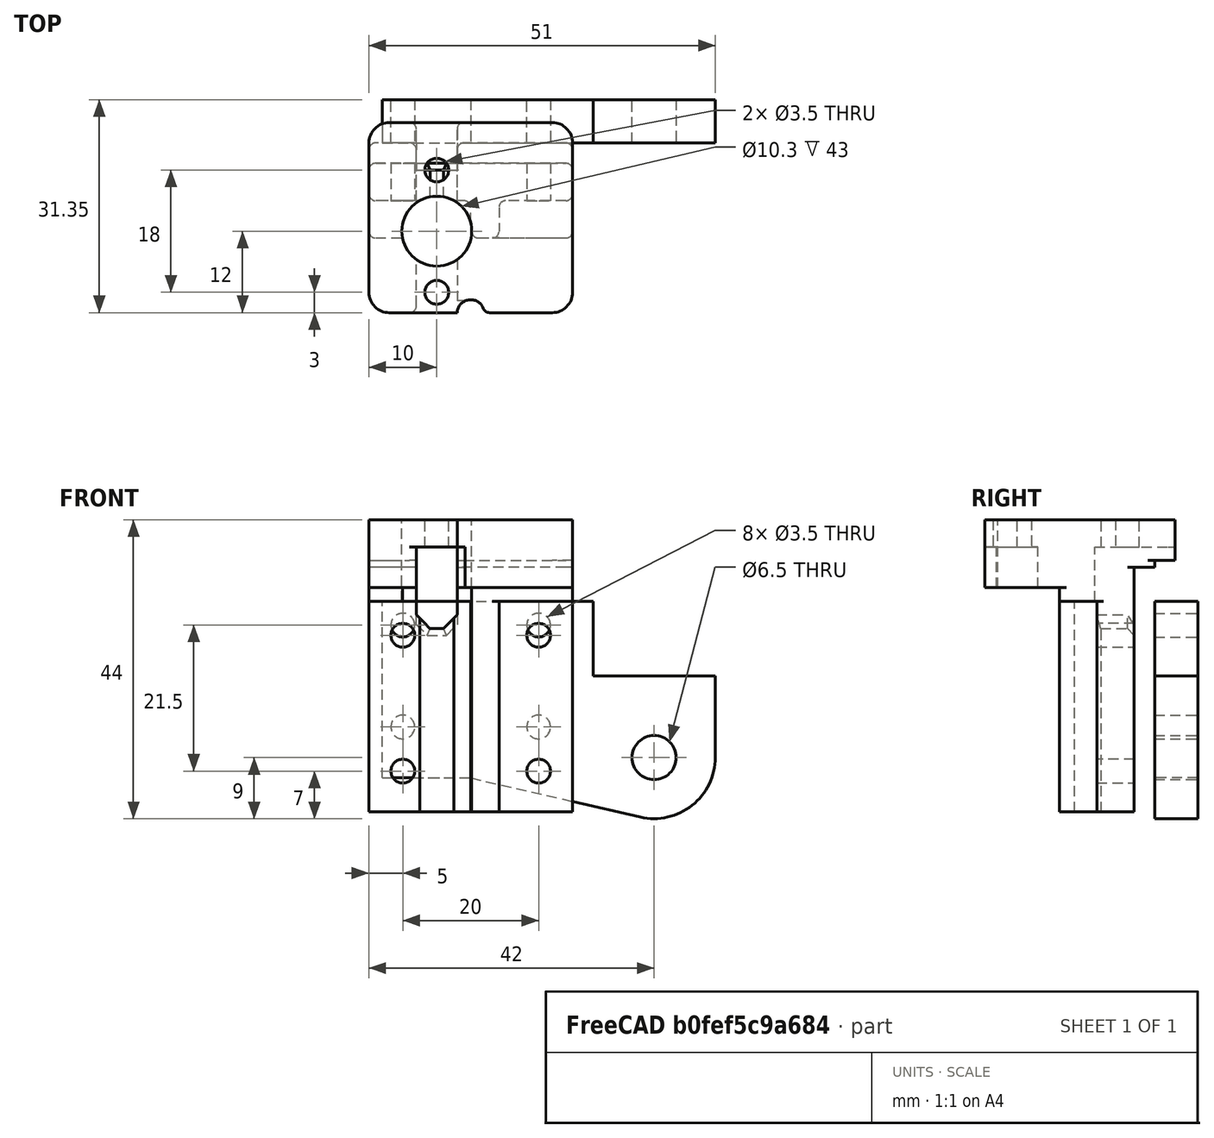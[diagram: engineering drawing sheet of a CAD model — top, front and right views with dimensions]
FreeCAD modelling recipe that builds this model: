
FCSTD DOCUMENT  (FreeCAD 0.19R)
Label: ZnutHolder_H3
License: All rights reserved
LicenseURL: http://en.wikipedia.org/wiki/All_rights_reserved
objects: PartDesign::Fillet×14, Sketcher::SketchObject×11, PartDesign::Pocket×8, PartDesign::Chamfer×3, PartDesign::Pad×2, PartDesign::Body×2, Mesh::Feature×1
note: 67 computed .brp shape members not serialized (recipe doc carries the construction recipe); baked Part::Feature solids carry a one-line shape summary decoded from their .brp

FEATURE [Sketcher::SketchObject] Sketch
  FullyConstrained = false
  MapMode = 5
  Placement = pos=(0,0,0) rot=(1,0,0;1.5708rad)
  Support = -> [XZ_Plane]
  sketch-geometry (14):
    g0: Circle CenterX=-10 CenterY=7.5 CenterZ=0 NormalX=0 NormalY=0 NormalZ=1 AngleXU=0 Radius=1.75
    g1: Circle CenterX=10 CenterY=7.5 CenterZ=0 NormalX=0 NormalY=0 NormalZ=1 AngleXU=0 Radius=1.75
    g2: Circle CenterX=-10 CenterY=-7.5 CenterZ=0 NormalX=0 NormalY=0 NormalZ=1 AngleXU=0 Radius=1.75
    g3: Circle CenterX=10 CenterY=-7.5 CenterZ=0 NormalX=0 NormalY=0 NormalZ=1 AngleXU=0 Radius=1.75
    g4: LineSegment StartX=-13 StartY=11 StartZ=0 EndX=18 EndY=11 EndZ=0
    g5: LineSegment StartX=18 StartY=11 StartZ=0 EndX=18 EndY=0 EndZ=0
    g6: LineSegment StartX=18 StartY=0 StartZ=0 EndX=36 EndY=0 EndZ=0
    g7: LineSegment StartX=36 StartY=0 StartZ=0 EndX=36 EndY=-12 EndZ=0
    g8: LineSegment StartX=-13 StartY=-15 StartZ=0 EndX=-13 EndY=11 EndZ=0
    g9: LineSegment StartX=-13 StartY=-15 StartZ=0 EndX=0 EndY=-15 EndZ=0
    g10: LineSegment StartX=0 StartY=-15 StartZ=0 EndX=24.9743 EndY=-20.7691 EndZ=0
    g11: ArcOfCircle CenterX=27 CenterY=-12 CenterZ=0 NormalX=0 NormalY=0 NormalZ=1 AngleXU=0 Radius=9 StartAngle=4.48537 EndAngle=6.28319
    g12: Circle CenterX=27 CenterY=-12 CenterZ=0 NormalX=0 NormalY=0 NormalZ=1 AngleXU=0 Radius=3.25
    g13: LineSegment StartX=19 StartY=18.0628 StartZ=0 EndX=19 EndY=-24.6673 EndZ=0
  constraints (37):
    c: Symmetric(g0,g1,g-2)
    c: Symmetric(g3,g2,g-2)
    c: Symmetric(g3,g1,g-1)
    c: Diameter(g0) = 3.5
    c: Equal(g0,g1)
    c: Equal(g0,g2)
    c: Equal(g0,g3)
    c: Distance(g1,g0) = 20
    c: Distance(g3,g1) = 15
    c: Horizontal(g4)
    c: Coincident(g4,g5)
    c: Vertical(g5)
    c: Coincident(g5,g6)
    c: Horizontal(g6)
    c: Coincident(g6,g7)
    c: Vertical(g7)
    c: Vertical(g8)
    c: DistanceX(g4) = 18
    c: DistanceX(g4) = -13
    c: Coincident(g8,g9)
    c: PointOnObject(g9,g-2)
    c: Horizontal(g9)
    c: Coincident(g9,g10)
    c: Tangent(g7,g11) = 1.5708
    c: Coincident(g11,g7)
    c: Tangent(g11,g10) = -1.5708
    c: Coincident(g12,g11)
    c: Diameter(g12) = 6.5
    c: Diameter(g11) = 18
    c: Vertical(g13)
    c: DistanceX(g13) = 19
    c: Distance(g11,g13) = 8
    c: Distance(g11,g6) = 12
    c: PointOnObject(g5,g-1)
    c: Coincident(g8,g4)
    c: DistanceY(g4) = 11
    c: DistanceY(g8) = -15
FEATURE [PartDesign::Pad] Pad
  Direction = (1,1,1)
  Length = 6.35
  Length2 = 100
  Placement = pos=(0,0,0) rot=(1,0,0;1.5708rad)
  Profile = -> Sketch
  Type = 0
FEATURE [PartDesign::Body] Body  label="Tab"
  Group = -> [Sketch,Pad]
  Origin = -> Origin
  Placement = pos=(0,6.35,0) rot=(0,0,1;0rad)
  Tip = -> Pad
FEATURE [Sketcher::SketchObject] Sketch005  label="body"
  FullyConstrained = true
  MapMode = 5
  Placement = pos=(0,0,0) rot=(0.57735,0.57735,0.57735;2.0944rad)
  Support = -> [YZ_Plane001]
  sketch-geometry (8):
    g0: LineSegment StartX=0 StartY=-20 StartZ=0 EndX=0 EndY=17 EndZ=0
    g1: LineSegment StartX=0 StartY=17 StartZ=0 EndX=3 EndY=17 EndZ=0
    g2: LineSegment StartX=3 StartY=17 StartZ=0 EndX=3 EndY=23 EndZ=0
    g3: LineSegment StartX=3 StartY=23 StartZ=0 EndX=-25 EndY=23 EndZ=0
    g4: LineSegment StartX=-25 StartY=23 StartZ=0 EndX=-25 EndY=13 EndZ=0
    g5: LineSegment StartX=-25 StartY=13 StartZ=0 EndX=-14 EndY=13 EndZ=0
    g6: LineSegment StartX=-14 StartY=13 StartZ=0 EndX=-14 EndY=-20 EndZ=0
    g7: LineSegment StartX=-14 StartY=-20 StartZ=0 EndX=0 EndY=-20 EndZ=0
  constraints (24):
    c: PointOnObject(g0,g-2)
    c: PointOnObject(g0,g-2)
    c: Coincident(g0,g1)
    c: Coincident(g1,g2)
    c: Vertical(g2)
    c: Coincident(g2,g3)
    c: Horizontal(g3)
    c: Coincident(g3,g4)
    c: Vertical(g4)
    c: Coincident(g4,g5)
    c: Horizontal(g5)
    c: Coincident(g5,g6)
    c: Vertical(g6)
    c: Coincident(g6,g7)
    c: Coincident(g7,g0)
    c: Horizontal(g7)
    c: Distance(g4) = 10
    c: DistanceY(g2) = 23
    c: DistanceX(g4) = -25
    c: Distance(g7) = 14
    c: DistanceY(g0) = -20
    c: DistanceX(g2) = 3
    c: Horizontal(g1)
    c: Distance(g2) = 6
FEATURE [PartDesign::Pad] Pad001
  Direction = (1,1,1)
  Length = 15
  Length2 = 15
  Placement = pos=(0,0,0) rot=(0.57735,0.57735,0.57735;2.0944rad)
  Profile = -> Sketch005
  Type = 4
FEATURE [Sketcher::SketchObject] Sketch007  label="ScrewHoles_rail"
  FullyConstrained = true
  MapMode = 5
  Placement = pos=(-6.2e-15,-14,2.33e-14) rot=(0.57735,0.57735,-0.57735;2.0944rad)
  sketch-geometry (8):
    g0: Circle CenterX=-6 CenterY=10 CenterZ=0 NormalX=0 NormalY=0 NormalZ=1 AngleXU=0 Radius=1.75
    g1: Circle CenterX=14 CenterY=10 CenterZ=0 NormalX=0 NormalY=0 NormalZ=1 AngleXU=0 Radius=1.75
    g2: Circle CenterX=-6 CenterY=-10 CenterZ=0 NormalX=0 NormalY=0 NormalZ=1 AngleXU=0 Radius=1.75
    g3: Circle CenterX=14 CenterY=-10 CenterZ=0 NormalX=0 NormalY=0 NormalZ=1 AngleXU=0 Radius=1.75
    g4: LineSegment StartX=-6 StartY=10 StartZ=0 EndX=-6 EndY=-10 EndZ=0
    g5: LineSegment StartX=-6 StartY=-10 StartZ=0 EndX=14 EndY=-10 EndZ=0
    g6: LineSegment StartX=14 StartY=-10 StartZ=0 EndX=14 EndY=10 EndZ=0
    g7: LineSegment StartX=14 StartY=10 StartZ=0 EndX=-6 EndY=10 EndZ=0
  constraints (19):
    c: Diameter(g0) = 3.5
    c: Equal(g0,g1)
    c: Equal(g0,g2)
    c: Equal(g0,g3)
    c: Coincident(g4,g0)
    c: Coincident(g4,g2)
    c: Coincident(g4,g5)
    c: Coincident(g5,g3)
    c: Coincident(g5,g6)
    c: Coincident(g6,g1)
    c: Coincident(g6,g7)
    c: Coincident(g7,g4)
    c: Equal(g4,g6)
    c: Equal(g7,g5)
    c: Distance(g7) = 20
    c: Distance(g6) = 20
    c: Perpendicular(g6,g5)
    c: Symmetric(g1,g3,g-1)
    c: DistanceX(g0) = -6
FEATURE [Sketcher::SketchObject] Sketch008  label="ScrewRelief"
  FullyConstrained = false
  MapMode = 5
  Placement = pos=(2.11e-14,-1.55e-14,-20) rot=(0.707107,0.707107,0;3.14159rad)
  sketch-geometry (8):
    g0: LineSegment StartX=-14.9077 StartY=0 StartZ=0 EndX=-8.5 EndY=0 EndZ=0
    g1: LineSegment StartX=-8.5 StartY=0 StartZ=0 EndX=-8.5 EndY=-16 EndZ=0
    g2: LineSegment StartX=-8.5 StartY=-16 StartZ=0 EndX=-14.9077 EndY=-16 EndZ=0
    g3: LineSegment StartX=-14.9077 StartY=-16 StartZ=0 EndX=-14.9077 EndY=0 EndZ=0
    g4: LineSegment StartX=-15.43 StartY=17.5817 StartZ=0 EndX=-8.5 EndY=17.5817 EndZ=0
    g5: LineSegment StartX=-8.5 StartY=17.5817 StartZ=0 EndX=-8.5 EndY=4.16376 EndZ=0
    g6: LineSegment StartX=-8.5 StartY=4.16376 StartZ=0 EndX=-15.43 EndY=4.16376 EndZ=0
    g7: LineSegment StartX=-15.43 StartY=4.16376 StartZ=0 EndX=-15.43 EndY=17.5817 EndZ=0
  constraints (20):
    c: Coincident(g0,g1)
    c: Coincident(g1,g2)
    c: Coincident(g2,g3)
    c: Coincident(g3,g0)
    c: Horizontal(g0)
    c: Horizontal(g2)
    c: Vertical(g1)
    c: Vertical(g3)
    c: Distance(g1) = 16
    c: DistanceY(g0) = 0
    c: DistanceX(g1) = -8.5
    c: Coincident(g4,g5)
    c: Coincident(g5,g6)
    c: Coincident(g6,g7)
    c: Coincident(g7,g4)
    c: Horizontal(g4)
    c: Horizontal(g6)
    c: Vertical(g5)
    c: Vertical(g7)
    c: DistanceX(g4) = -8.5
FEATURE [Sketcher::SketchObject] Sketch011  label="Carriage"
  FullyConstrained = false
  MapMode = 5
  Placement = pos=(0,0,0) rot=(1,0,0;1.5708rad)
  Support = -> [XZ_Plane001]
  sketch-geometry (8):
    g0: LineSegment StartX=-19.4447 StartY=17.5 StartZ=0 EndX=25.2288 EndY=17.5 EndZ=0
    g1: LineSegment StartX=25.2288 StartY=17.5 StartZ=0 EndX=25.2288 EndY=-17.5 EndZ=0
    g2: LineSegment StartX=25.2288 StartY=-17.5 StartZ=0 EndX=-19.4447 EndY=-17.5 EndZ=0
    g3: LineSegment StartX=-19.4447 StartY=-17.5 StartZ=0 EndX=-19.4447 EndY=17.5 EndZ=0
    g4: LineSegment StartX=-16.964 StartY=15 StartZ=0 EndX=21.1039 EndY=15 EndZ=0
    g5: LineSegment StartX=21.1039 StartY=15 StartZ=0 EndX=21.1039 EndY=-15 EndZ=0
    g6: LineSegment StartX=21.1039 StartY=-15 StartZ=0 EndX=-16.964 EndY=-15 EndZ=0
    g7: LineSegment StartX=-16.964 StartY=-15 StartZ=0 EndX=-16.964 EndY=15 EndZ=0
  constraints (19):
    c: Coincident(g0,g1)
    c: Coincident(g1,g2)
    c: Coincident(g2,g3)
    c: Coincident(g3,g0)
    c: Horizontal(g0)
    c: Horizontal(g2)
    c: Vertical(g1)
    c: Vertical(g3)
    c: DistanceY(g0) = 17.5
    c: Distance(g1) = 35
    c: Coincident(g4,g5)
    c: Coincident(g5,g6)
    c: Coincident(g6,g7)
    c: Coincident(g7,g4)
    c: Horizontal(g4)
    c: Horizontal(g6)
    c: Vertical(g7)
    c: Distance(g5) = 30
    c: Symmetric(g4,g5,g-1)
FEATURE [Sketcher::SketchObject] Sketch012  label="NutHole"
  FullyConstrained = true
  MapMode = 5
  Placement = pos=(-8.9e-15,1.28e-14,23) rot=(0,0,-1;1.5708rad)
  Support = -> [Pad001]
  sketch-geometry (1):
    g0: Circle CenterX=13 CenterY=-5 CenterZ=0 NormalX=0 NormalY=0 NormalZ=1 AngleXU=0 Radius=5.15
  constraints (3):
    c: Diameter(g0) = 10.3
    c: DistanceY(g0) = -5
    c: DistanceX(g0) = 13
FEATURE [Sketcher::SketchObject] Sketch013  label="Nutscrews"
  FullyConstrained = true
  MapMode = 5
  Placement = pos=(-7.2e-14,3.9e-14,35) rot=(0,0,-1;1.5708rad)
  sketch-geometry (2):
    g0: Circle CenterX=4 CenterY=-5 CenterZ=0 NormalX=0 NormalY=0 NormalZ=1 AngleXU=0 Radius=1.75
    g1: Circle CenterX=22 CenterY=-5 CenterZ=0 NormalX=0 NormalY=0 NormalZ=1 AngleXU=0 Radius=1.75
  constraints (6):
    c: DistanceY(g1) = -5
    c: DistanceY(g0) = -5
    c: DistanceX(g1) = 22
    c: DistanceX(g0) = 4
    c: Diameter(g1) = 3.5
    c: Equal(g1,g0)
FEATURE [Sketcher::SketchObject] Sketch014  label="tunnel"
  ExternalGeometry = -> [Pad001]
  FullyConstrained = true
  MapMode = 5
  Placement = pos=(-1.11e-14,-25,8.3e-15) rot=(-0.57735,-0.57735,0.57735;4.18879rad)
  Support = -> [Pad001]
  sketch-geometry (4):
    g0: LineSegment StartX=-19 StartY=-2 StartZ=0 EndX=-7 EndY=-2 EndZ=0
    g1: LineSegment StartX=-7 StartY=-2 StartZ=0 EndX=-7 EndY=-8 EndZ=0
    g2: LineSegment StartX=-7 StartY=-8 StartZ=0 EndX=-19 EndY=-8 EndZ=0
    g3: LineSegment StartX=-19 StartY=-8 StartZ=0 EndX=-19 EndY=-2 EndZ=0
  constraints (12):
    c: Coincident(g0,g1)
    c: Coincident(g1,g2)
    c: Coincident(g2,g3)
    c: Coincident(g3,g0)
    c: Horizontal(g0)
    c: Horizontal(g2)
    c: Vertical(g1)
    c: Vertical(g3)
    c: Distance(g1) = 6
    c: DistanceY(g0) = -2
    c: Distance(g0) = 12
    c: Distance(g0,g-3) = 4
FEATURE [PartDesign::Pocket] Pocket
  BaseFeature = -> Pad001
  Length = 5
  Length2 = 100
  Placement = pos=(0,0,0) rot=(0.57735,0.57735,0.57735;2.0944rad)
  Profile = -> Sketch014
  Type = 1
FEATURE [Sketcher::SketchObject] Sketch015  label="backpocket"
  FullyConstrained = true
  MapMode = 5
  Placement = pos=(0,-8e-15,0) rot=(0.57735,0.57735,0.57735;4.18879rad)
  sketch-geometry (4):
    g0: LineSegment StartX=-34.47 StartY=20 StartZ=0 EndX=16 EndY=20 EndZ=0
    g1: LineSegment StartX=16 StartY=20 StartZ=0 EndX=16 EndY=-20 EndZ=0
    g2: LineSegment StartX=16 StartY=-20 StartZ=0 EndX=-34.47 EndY=-20 EndZ=0
    g3: LineSegment StartX=-34.47 StartY=-20 StartZ=0 EndX=-34.47 EndY=20 EndZ=0
  constraints (11):
    c: Coincident(g0,g1)
    c: Coincident(g1,g2)
    c: Coincident(g2,g3)
    c: Coincident(g3,g0)
    c: Horizontal(g0)
    c: Horizontal(g2)
    c: Vertical(g1)
    c: Distance(g3) = 40
    c: Symmetric(g2,g0,g-1)
    c: Distance(g0) = 50.47
    c: DistanceX(g0) = 16
FEATURE [Sketcher::SketchObject] Sketch018  label="Seamnotch"
  FullyConstrained = false
  MapMode = 5
  Placement = pos=(-9.8e-15,3.48e-14,35) rot=(0,0,-1;1.5708rad)
  sketch-geometry (1):
    g0: Circle CenterX=25.0896 CenterY=0 CenterZ=0 NormalX=0 NormalY=0 NormalZ=1 AngleXU=0 Radius=2
  constraints (2):
    c: PointOnObject(g0,g-1)
    c: Diameter(g0) = 4
FEATURE [PartDesign::Pocket] Pocket001
  BaseFeature = -> Pocket
  Length = 21
  Length2 = 100
  Placement = pos=(0,0,0) rot=(0.57735,0.57735,0.57735;2.0944rad)
  Profile = -> Sketch013
  Type = 0
FEATURE [PartDesign::Pocket] Pocket002
  BaseFeature = -> Pocket001
  Length = 15
  Length2 = 100
  Placement = pos=(0,0,0) rot=(0.57735,0.57735,0.57735;2.0944rad)
  Profile = -> Sketch012
  Type = 1
FEATURE [PartDesign::Pocket] Pocket003
  BaseFeature = -> Pocket002
  Length = 5
  Length2 = 100
  Placement = pos=(0,0,0) rot=(0.57735,0.57735,0.57735;2.0944rad)
  Profile = -> Sketch007
  Type = 1
FEATURE [PartDesign::Pocket] Pocket004
  BaseFeature = -> Pocket003
  Length = 31
  Length2 = 100
  Placement = pos=(0,0,0) rot=(0.57735,0.57735,0.57735;2.0944rad)
  Profile = -> Sketch008
  Type = 0
FEATURE [PartDesign::Pocket] Pocket005
  BaseFeature = -> Pocket004
  Length = 5
  Length2 = 100
  Placement = pos=(0,0,0) rot=(0.57735,0.57735,0.57735;2.0944rad)
  Profile = -> Sketch018
  Type = 1
FEATURE [Sketcher::SketchObject] Sketch020  label="minitri"
  FullyConstrained = false
  MapMode = 5
  Placement = pos=(-3.1e-14,1.59e-14,13) rot=(0.707107,0.707107,0;3.14159rad)
  Support = -> [Pocket005]
  sketch-geometry (4):
    g0: LineSegment StartX=-25.5214 StartY=0 StartZ=0 EndX=-23.2601 EndY=0 EndZ=0
    g1: LineSegment StartX=-23.2601 StartY=0 StartZ=0 EndX=-23.2601 EndY=-2.34206 EndZ=0
    g2: LineSegment StartX=-23.2601 StartY=-2.34206 StartZ=0 EndX=-25.5214 EndY=-2.34206 EndZ=0
    g3: LineSegment StartX=-25.5214 StartY=-2.34206 StartZ=0 EndX=-25.5214 EndY=0 EndZ=0
  constraints (9):
    c: Coincident(g0,g1)
    c: Coincident(g1,g2)
    c: Coincident(g2,g3)
    c: Coincident(g3,g0)
    c: Horizontal(g0)
    c: Horizontal(g2)
    c: Vertical(g1)
    c: Vertical(g3)
    c: PointOnObject(g0,g-1)
FEATURE [PartDesign::Pocket] Pocket006
  BaseFeature = -> Pocket005
  Length = 6
  Length2 = 100
  Placement = pos=(0,0,0) rot=(0.57735,0.57735,0.57735;2.0944rad)
  Profile = -> Sketch020
  Type = 0
FEATURE [PartDesign::Pocket] Pocket007
  BaseFeature = -> Pocket006
  Length = 3
  Length2 = 100
  Placement = pos=(0,0,0) rot=(0.57735,0.57735,0.57735;2.0944rad)
  Profile = -> Sketch015
  Type = 0
FEATURE [PartDesign::Chamfer] Chamfer
  Angle = 45
  Base = -> Pocket007 [Edge23]
  BaseFeature = -> Pocket007
  ChamferType = 0
  FlipDirection = false
  Placement = pos=(0,0,0) rot=(0.57735,0.57735,0.57735;2.0944rad)
  Size = 2
  Size2 = 1
  SupportTransform = false
FEATURE [PartDesign::Chamfer] Chamfer001
  Angle = 45
  Base = -> Chamfer [Edge64]
  BaseFeature = -> Chamfer
  ChamferType = 0
  FlipDirection = false
  Placement = pos=(0,0,0) rot=(0.57735,0.57735,0.57735;2.0944rad)
  Size = 2
  Size2 = 1
  SupportTransform = false
FEATURE [PartDesign::Chamfer] Chamfer002
  Angle = 45
  Base = -> Chamfer001 [Edge2,Edge1,Edge3]
  BaseFeature = -> Chamfer001
  ChamferType = 0
  FlipDirection = false
  Placement = pos=(0,0,0) rot=(0.57735,0.57735,0.57735;2.0944rad)
  Size = 1
  Size2 = 1
  SupportTransform = false
FEATURE [PartDesign::Fillet] Fillet
  Base = -> Chamfer002 [Edge67,Edge37,Edge69,Edge39]
  BaseFeature = -> Chamfer002
  Placement = pos=(0,0,0) rot=(0.57735,0.57735,0.57735;2.0944rad)
  Radius = 3
  SupportTransform = false
FEATURE [PartDesign::Fillet] Fillet001
  Base = -> Fillet [Edge95,Edge22]
  BaseFeature = -> Fillet
  Placement = pos=(0,0,0) rot=(0.57735,0.57735,0.57735;2.0944rad)
  Radius = 1
  SupportTransform = false
FEATURE [PartDesign::Fillet] Fillet002
  Base = -> Fillet001 [Edge3]
  BaseFeature = -> Fillet001
  Placement = pos=(0,0,0) rot=(0.57735,0.57735,0.57735;2.0944rad)
  Radius = 1
  SupportTransform = false
FEATURE [PartDesign::Fillet] Fillet003
  Base = -> Fillet002 [Edge6,Edge39]
  BaseFeature = -> Fillet002
  Placement = pos=(0,0,0) rot=(0.57735,0.57735,0.57735;2.0944rad)
  Radius = 1
  SupportTransform = false
FEATURE [PartDesign::Fillet] Fillet004
  Base = -> Fillet003 [Edge159]
  BaseFeature = -> Fillet003
  Placement = pos=(0,0,0) rot=(0.57735,0.57735,0.57735;2.0944rad)
  Radius = 1
  SupportTransform = false
FEATURE [PartDesign::Fillet] Fillet005
  Base = -> Fillet004 [Edge111]
  BaseFeature = -> Fillet004
  Placement = pos=(0,0,0) rot=(0.57735,0.57735,0.57735;2.0944rad)
  Radius = 1
  SupportTransform = false
FEATURE [PartDesign::Fillet] Fillet006
  Base = -> Fillet005 [Edge71]
  BaseFeature = -> Fillet005
  Placement = pos=(0,0,0) rot=(0.57735,0.57735,0.57735;2.0944rad)
  Radius = 1
  SupportTransform = false
FEATURE [PartDesign::Fillet] Fillet007
  Base = -> Fillet006 [Edge63]
  BaseFeature = -> Fillet006
  Placement = pos=(0,0,0) rot=(0.57735,0.57735,0.57735;2.0944rad)
  Radius = 1
  SupportTransform = false
FEATURE [PartDesign::Fillet] Fillet008
  Base = -> Fillet007 [Edge72,Edge44]
  BaseFeature = -> Fillet007
  Placement = pos=(0,0,0) rot=(0.57735,0.57735,0.57735;2.0944rad)
  Radius = 1
  SupportTransform = false
FEATURE [PartDesign::Fillet] Fillet009
  Base = -> Fillet008 [Edge158,Edge145]
  BaseFeature = -> Fillet008
  Placement = pos=(0,0,0) rot=(0.57735,0.57735,0.57735;2.0944rad)
  Radius = 1
  SupportTransform = false
FEATURE [PartDesign::Fillet] Fillet010
  Base = -> Fillet009 [Edge6,Edge80]
  BaseFeature = -> Fillet009
  Placement = pos=(0,0,0) rot=(0.57735,0.57735,0.57735;2.0944rad)
  Radius = 1
  SupportTransform = false
FEATURE [PartDesign::Fillet] Fillet011
  Base = -> Fillet010 [Edge198]
  BaseFeature = -> Fillet010
  Placement = pos=(0,0,0) rot=(0.57735,0.57735,0.57735;2.0944rad)
  Radius = 1
  SupportTransform = false
FEATURE [PartDesign::Fillet] Fillet012
  Base = -> Fillet011 [Edge159]
  BaseFeature = -> Fillet011
  Placement = pos=(0,0,0) rot=(0.57735,0.57735,0.57735;2.0944rad)
  Radius = 1
  SupportTransform = false
FEATURE [PartDesign::Fillet] Fillet013
  Base = -> Fillet012 [Edge200]
  BaseFeature = -> Fillet012
  Placement = pos=(0,0,0) rot=(0.57735,0.57735,0.57735;2.0944rad)
  Radius = 1
  SupportTransform = false
FEATURE [PartDesign::Body] Body001  label="LeadScrewMount"
  Group = -> [Sketch005,Pad001,Sketch007,Sketch008,Sketch011,Sketch012,Sketch013,Sketch014,Pocket,Sketch015,Sketch018,Sketch020,Pocket001,Pocket002,Pocket003,Pocket004,Pocket005,Pocket006,Pocket007,Chamfer,Chamfer001,Chamfer002,Fillet,Fillet001,Fillet002,Fillet003,Fillet004,Fillet005,Fillet006,Fillet007,Fillet008,Fillet009,Fillet010,Fillet011,Fillet012,Fillet013]
  Origin = -> Origin001
  Tip = -> Fillet013
FEATURE [Mesh::Feature] Mesh  label="Fillet013 (Meshed)"
